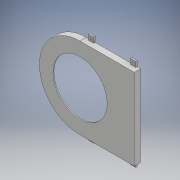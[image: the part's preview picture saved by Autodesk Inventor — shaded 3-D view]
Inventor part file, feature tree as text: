
AUTODESK INVENTOR PART (.ipt)
format: ipt  version: 2018 (Build 220112000, 112)  size: 162,816 bytes
history: native  units: mm
features: extrude x3, sketch x3
ambient origin geometry x8: Origin, YZ Plane, XZ Plane, XY Plane, X Axis, Y Axis, Z Axis, Center Point
bodies: Solide1 (feature_tree)
feature tree (6):
  extrude  "Extrusion1"  Depth=120.0mm
  extrude  "Extrusion2"  Depth=120.0mm
  extrude  "Extrusion3"  Depth=180.0mm
  sketch  "Esquisse1"
  sketch  "Esquisse2"
  sketch  "Esquisse3"
